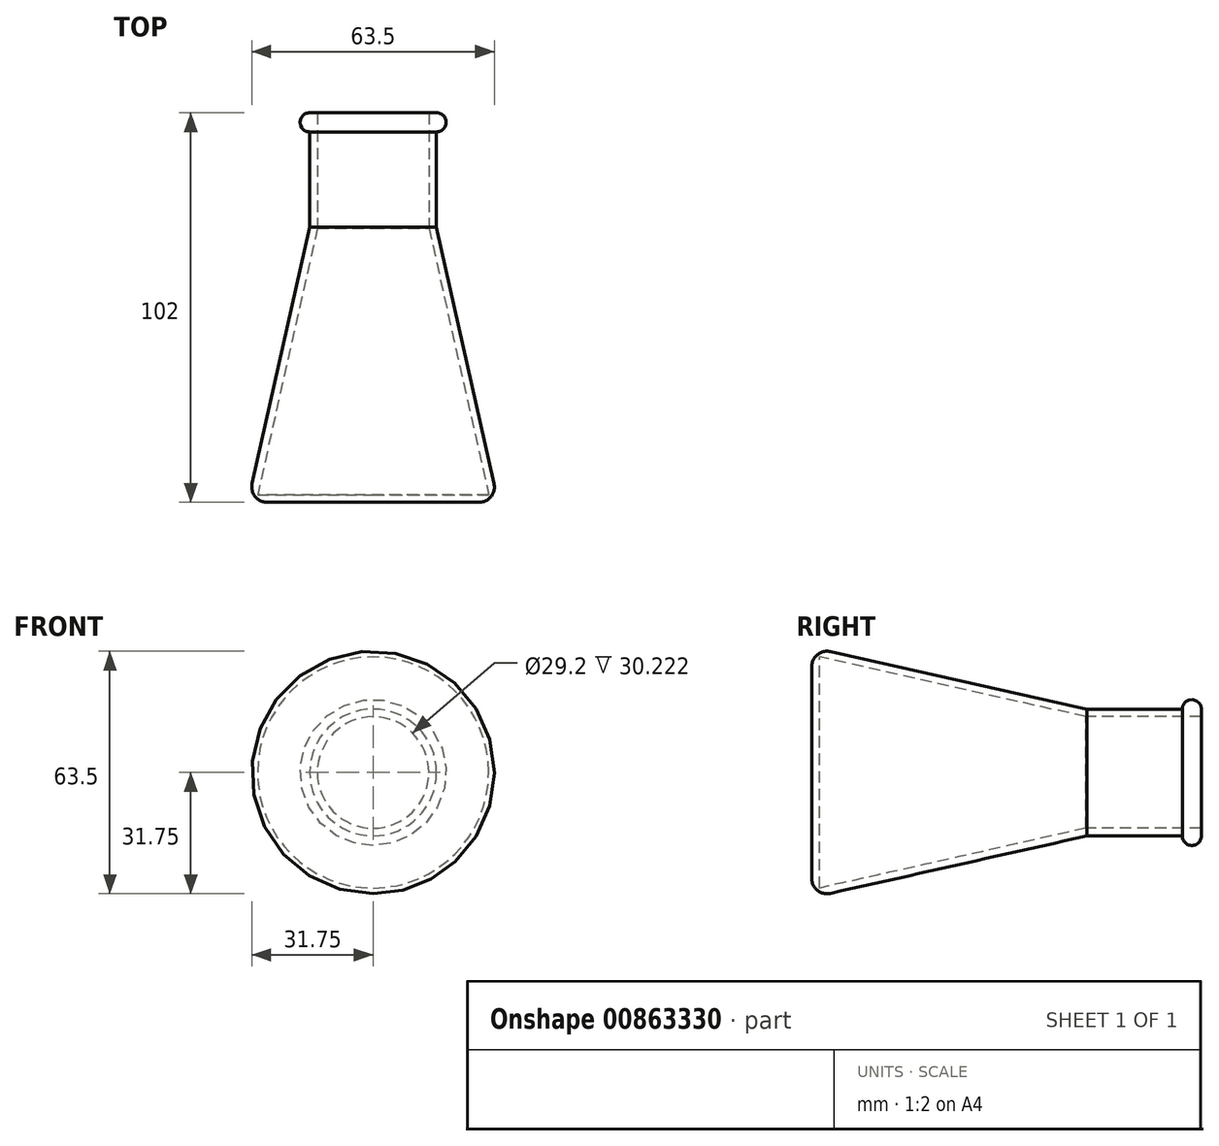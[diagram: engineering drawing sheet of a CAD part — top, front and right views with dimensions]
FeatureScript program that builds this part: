
annotation { "Feature Type Name" : "Feature", "Feature Type Description" : "" }
export const myFeature = defineFeature(function(context is Context, id is Id, definition is map)
    precondition{}
    {
        {
            var Q0;
            Q0=qCreatedBy(makeId("Top.planeOp"),FACE);
            var sketch = newSketch(context, id + "F0", { "sketchPlane" : qUnion([Q0])});
            skLineSegment(sketch, "E0", {"start": v(31.66, 4.88) * mm, "end": v(16.6, 72) * mm});
            skArc(sketch, "E1", {"start": v(16.6, 97) * mm, "mid": v(19.1, 99.5) * mm, "end": v(16.6, 102) * mm});
            skLineSegment(sketch, "E2.0", {"start": v(14.6, 71.78) * mm, "end": v(14.6, 102) * mm});
            skLineSegment(sketch, "E2.1", {"start": v(30.25, 2) * mm, "end": v(14.6, 71.78) * mm});
            skLineSegment(sketch, "E3", {"start": v(30.25, 2) * mm, "end": v(0, 2) * mm});
            skPoint(sketch, "E4.visualSharp", {"position": v(32.75, 0) * mm});
            skArc(sketch, "E4.filletArc", {"start": v(27.75, 0) * mm, "mid": v(30.88, 1.5) * mm, "end": v(31.66, 4.88) * mm});
            skLineSegment(sketch, "E5", {"start": v(14.6, 102) * mm, "end": v(16.6, 102) * mm});
            skLineSegment(sketch, "E6", {"start": v(16.6, 97) * mm, "end": v(16.6, 72) * mm});
            skLineSegment(sketch, "E7", {"start": v(0, 2) * mm, "end": v(0, 0) * mm});
            skLineSegment(sketch, "E8", {"start": v(0, 2) * mm, "end": v(0, 35.01) * mm});
            skLineSegment(sketch, "E9", {"start": v(0, 0) * mm, "end": v(27.75, 0) * mm});
            skSolve(sketch);
        }
        {
            var Q0;
            Q0 = qSketchRegion(id + "F0", true);
            var Q1;
            Q1=sQuery(id+"F0.wireOp",EDGE,"E8");
            revolve(context, id + "F1", {"surfaceOperationType" : NewSurfaceOperationType.NEW, "entities" : qUnion([Q0]), "axis" : qUnion([Q1]), "revolveType" : RevolveType.FULL});
        }
    });
